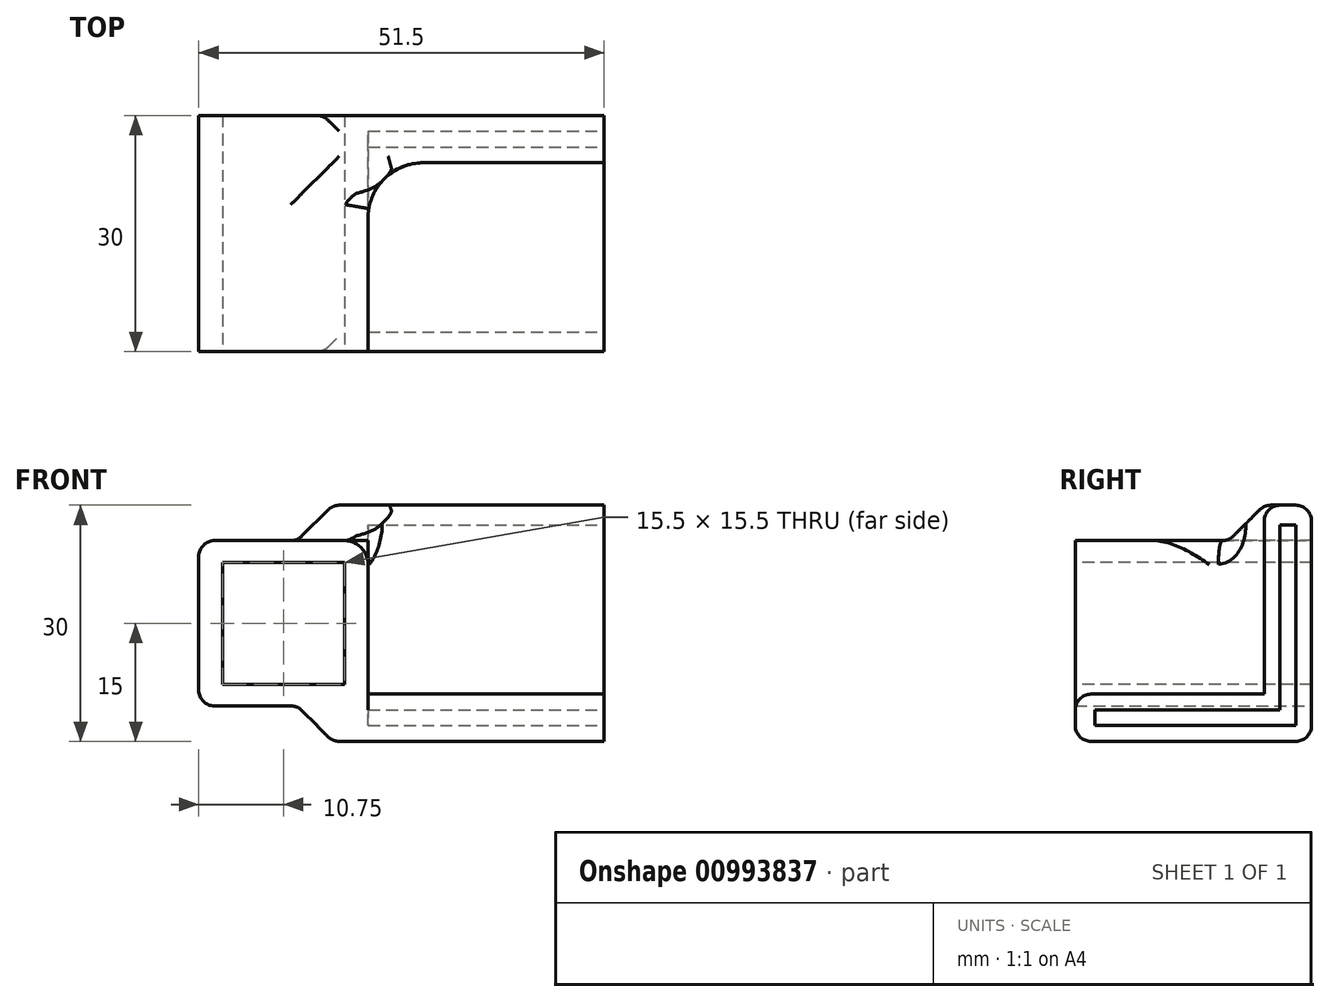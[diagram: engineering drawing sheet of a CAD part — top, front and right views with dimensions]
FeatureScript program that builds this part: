
annotation { "Feature Type Name" : "Feature", "Feature Type Description" : "" }
export const myFeature = defineFeature(function(context is Context, id is Id, definition is map)
    precondition{}
    {
        {
            var Q0;
            Q0=qCreatedBy(makeId("Top.planeOp"),FACE);
            var sketch = newSketch(context, id + "F0", { "sketchPlane" : qUnion([Q0])});
            skLineSegment(sketch, "E0", {"start": v(18, -44.27) * mm, "end": v(24, -44.27) * mm});
            skLineSegment(sketch, "E1", {"start": v(24, -44.27) * mm, "end": v(24, -14.27) * mm});
            skLineSegment(sketch, "E2", {"start": v(24, -14.27) * mm, "end": v(-12, -14.27) * mm});
            skLineSegment(sketch, "E3", {"start": v(-12, -14.27) * mm, "end": v(-12, -44.27) * mm});
            skLineSegment(sketch, "E4", {"start": v(-6, -44.27) * mm, "end": v(-6, -20.27) * mm});
            skLineSegment(sketch, "E5", {"start": v(-6, -20.27) * mm, "end": v(24, -20.27) * mm});
            skLineSegment(sketch, "E6", {"start": v(18, -44.27) * mm, "end": v(-12, -44.27) * mm});
            skSolve(sketch);
        }
        {
            var Q0;
            {var subQ2=sQuery(id+"F0.wireOp",EDGE,"E0");Q0=makeQuery(id+"F0.imprint","IMPRINT",FACE,{"disambiguationData":[TD([[makeQuery(id+"F0.imprint","IMPRINT",EDGE,{"derivedFrom":subQ2}),1.0]])]});}
            extrude(context, id + "F1", {"entities" : qUnion([Q0]), "depth" : 6 * mm, "offsetDistance" : 25 * mm});
        }
        {
            var Q0;
            {var subQ1=sQuery(id+"F0.wireOp",EDGE,"E2");Q0=makeQuery(id+"F0.imprint","IMPRINT",FACE,{"disambiguationData":[TD([[makeQuery(id+"F0.imprint","IMPRINT",EDGE,{"derivedFrom":subQ1}),1.0]])]});}
            extrude(context, id + "F2", {"entities" : qUnion([Q0]), "operationType" : NewBodyOperationType.ADD, "depth" : 30 * mm, "offsetDistance" : 25 * mm});
        }
        {
            var Q0;
            {var subQ0=sQuery(id+"F0.wireOp",EDGE,"E1");Q0=makeQuery(id+"F2.boolean.opBoolean","MERGE",FACE,{"derivedFrom":[makeQuery(id+"F1.opExtrude","SWEPT_FACE",FACE,{"disambiguationData":[OSD([subQ0])]}),makeQuery(id+"F2.opExtrude","SWEPT_FACE",FACE,{"disambiguationData":[OSD([subQ0])]})]});}
            var sketch = newSketch(context, id + "F3", { "sketchPlane" : qUnion([Q0])});
            skLineSegment(sketch, "E7", {"start": v(-41.77, 4) * mm, "end": v(-18.27, 4) * mm});
            skLineSegment(sketch, "E8", {"start": v(-18.27, 4) * mm, "end": v(-18.27, 27.5) * mm});
            skLineSegment(sketch, "E9", {"start": v(-18.27, 27.5) * mm, "end": v(-16.27, 27.5) * mm});
            skLineSegment(sketch, "E10", {"start": v(-16.27, 27.5) * mm, "end": v(-16.27, 2) * mm});
            skLineSegment(sketch, "E11", {"start": v(-16.27, 2) * mm, "end": v(-41.77, 2) * mm});
            skLineSegment(sketch, "E12", {"start": v(-41.77, 2) * mm, "end": v(-41.77, 4) * mm});
            skSolve(sketch);
        }
        {
            var Q0;
            Q0=makeQuery(id+"F3.imprint","IMPRINT",FACE,{"disambiguationData":[TD([[makeQuery(id+"F3.imprint","IMPRINT",EDGE,{"derivedFrom":sQuery(id+"F3.wireOp",EDGE,"E7")}),-1.0]])]});
            extrude(context, id + "F4", {"entities" : qUnion([Q0]), "operationType" : NewBodyOperationType.REMOVE, "oppositeDirection" : true, "depth" : 30 * mm, "offsetDistance" : 25 * mm});
        }
        {
            var Q0;
            Q0=makeQuery(id+"F2.opExtrude","SWEPT_FACE",FACE,{"disambiguationData":[OSD([sQuery(id+"F0.wireOp",EDGE,"E3")])]});
            extrude(context, id + "F5", {"entities" : qUnion([Q0]), "operationType" : NewBodyOperationType.ADD, "depth" : 20 * mm, "offsetDistance" : 25 * mm});
        }
        {
            var Q0;
            {var subQ0=sQuery(id+"F0.wireOp",EDGE,"E6");Q0=makeQuery(id+"F5.boolean.opBoolean","MERGE",FACE,{"derivedFrom":[makeQuery(id+"F2.boolean.opBoolean","MERGE",FACE,{"derivedFrom":[makeQuery(id+"F1.opExtrude","SWEPT_FACE",FACE,{"disambiguationData":[OSD([sQuery(id+"F0.wireOp",EDGE,"E0"),subQ0])]}),makeQuery(id+"F2.opExtrude","SWEPT_FACE",FACE,{"disambiguationData":[OSD([subQ0])]})]}),makeQuery(id+"F5.opExtrude","SWEPT_FACE",FACE,{"disambiguationData":[OSD([sQuery(id+"F0.wireOp",EDGE,"E3"),subQ0])]})]});}
            var sketch = newSketch(context, id + "F6", { "sketchPlane" : qUnion([Q0])});
            skLineSegment(sketch, "E13.bottom", {"start": v(-9, 7.25) * mm, "end": v(-24.5, 7.25) * mm});
            skLineSegment(sketch, "E13.top", {"start": v(-9, 22.75) * mm, "end": v(-24.5, 22.75) * mm});
            skLineSegment(sketch, "E13.left", {"start": v(-9, 7.25) * mm, "end": v(-9, 22.75) * mm});
            skLineSegment(sketch, "E13.right", {"start": v(-24.5, 7.25) * mm, "end": v(-24.5, 22.75) * mm});
            skPoint(sketch, "E13.middle", {"position": v(-16.75, 15) * mm});
            skLineSegment(sketch, "E14", {"start": v(-10.5, 25.5) * mm, "end": v(-10.5, 30) * mm});
            skLineSegment(sketch, "E15", {"start": v(-10.5, 25.5) * mm, "end": v(-27.5, 25.5) * mm});
            skLineSegment(sketch, "E16", {"start": v(-27.5, 25.5) * mm, "end": v(-27.5, 4.5) * mm});
            skLineSegment(sketch, "E17", {"start": v(-27.5, 4.5) * mm, "end": v(-10.5, 4.5) * mm});
            skLineSegment(sketch, "E18", {"start": v(-10.5, 4.5) * mm, "end": v(-10.5, 0) * mm});
            skLineSegment(sketch, "E19", {"start": v(-10.5, 0) * mm, "end": v(-32, 0) * mm});
            skLineSegment(sketch, "E20", {"start": v(-32, 0) * mm, "end": v(-32, 30) * mm});
            skLineSegment(sketch, "E21", {"start": v(-32, 30) * mm, "end": v(-10.5, 30) * mm});
            skLineSegment(sketch, "E22", {"start": v(-10.5, 25.5) * mm, "end": v(-6, 25.5) * mm});
            skLineSegment(sketch, "E23", {"start": v(-6, 25.5) * mm, "end": v(-6, 30) * mm});
            skLineSegment(sketch, "E24", {"start": v(-6, 30) * mm, "end": v(-10.5, 30) * mm});
            skSolve(sketch);
        }
        {
            var Q0;
            Q0=makeQuery(id+"F6.imprint","IMPRINT",FACE,{"disambiguationData":[TD([[makeQuery(id+"F6.imprint","IMPRINT",EDGE,{"derivedFrom":sQuery(id+"F6.wireOp",EDGE,"E13.bottom")}),-1.0]])]});
            var Q1;
            {var subQ0=sQuery(id+"F0.wireOp",EDGE,"E2");Q1=makeQuery(id+"F5.boolean.opBoolean","MERGE",FACE,{"derivedFrom":[makeQuery(id+"F2.opExtrude","SWEPT_FACE",FACE,{"disambiguationData":[OSD([subQ0])]}),makeQuery(id+"F5.opExtrude","SWEPT_FACE",FACE,{"disambiguationData":[OSD([subQ0,sQuery(id+"F0.wireOp",EDGE,"E3")])]})]});}
            extrude(context, id + "F7", {"entities" : qUnion([Q0]), "operationType" : NewBodyOperationType.REMOVE, "endBound" : BoundingType.UP_TO_SURFACE, "oppositeDirection" : true, "depth" : 25 * mm, "endBoundEntityFace" : qUnion([Q1]), "offsetDistance" : 25 * mm});
        }
        {
            var Q0;
            Q0=makeQuery(id+"F6.imprint","IMPRINT",FACE,{"disambiguationData":[TD([[makeQuery(id+"F6.imprint","IMPRINT",EDGE,{"derivedFrom":sQuery(id+"F6.wireOp",EDGE,"E14")}),1.0]])]});
            var Q1;
            {var subQ0=sQuery(id+"F0.wireOp",EDGE,"E2");Q1=makeQuery(id+"F5.boolean.opBoolean","MERGE",FACE,{"derivedFrom":[makeQuery(id+"F2.opExtrude","SWEPT_FACE",FACE,{"disambiguationData":[OSD([subQ0])]}),makeQuery(id+"F5.opExtrude","SWEPT_FACE",FACE,{"disambiguationData":[OSD([subQ0,sQuery(id+"F0.wireOp",EDGE,"E3")])]})]});}
            extrude(context, id + "F8", {"entities" : qUnion([Q0]), "operationType" : NewBodyOperationType.REMOVE, "endBound" : BoundingType.UP_TO_SURFACE, "oppositeDirection" : true, "depth" : 25 * mm, "endBoundEntityFace" : qUnion([Q1]), "offsetDistance" : 25 * mm});
        }
        {
            var Q0;
            Q0=makeQuery(id+"F6.imprint","IMPRINT",FACE,{"disambiguationData":[TD([[makeQuery(id+"F6.imprint","IMPRINT",EDGE,{"derivedFrom":sQuery(id+"F6.wireOp",EDGE,"E14")}),-1.0]])]});
            var Q1;
            Q1=makeQuery(id+"F2.opExtrude","SWEPT_FACE",FACE,{"disambiguationData":[OSD([sQuery(id+"F0.wireOp",EDGE,"E5")])]});
            extrude(context, id + "F9", {"entities" : qUnion([Q0]), "operationType" : NewBodyOperationType.REMOVE, "endBound" : BoundingType.UP_TO_SURFACE, "oppositeDirection" : true, "depth" : 22 * mm, "endBoundEntityFace" : qUnion([Q1]), "offsetDistance" : 25 * mm});
        }
        {
            var Q0;
            Q0=makeQuery(id+"F8.boolean.opBoolean","COPY",EDGE,{"derivedFrom":makeQuery(id+"F8.opExtrude","SWEPT_EDGE",EDGE,{"disambiguationData":[OSD([sQuery(id+"F6.wireOp",EDGE,"E14"),sQuery(id+"F6.wireOp",EDGE,"E15"),sQuery(id+"F6.wireOp",EDGE,"E22")])]})});
            var Q1;
            Q1=makeQuery(id+"F8.boolean.opBoolean","COPY",EDGE,{"derivedFrom":makeQuery(id+"F8.opExtrude","SWEPT_EDGE",EDGE,{"disambiguationData":[OSD([sQuery(id+"F6.wireOp",EDGE,"E17"),sQuery(id+"F6.wireOp",EDGE,"E18")])]})});
            var Q2;
            Q2=makeQuery(id+"F9.boolean.opBoolean","COPY",EDGE,{"derivedFrom":makeQuery(id+"F9.opExtrude","CAP_EDGE",EDGE,{"disambiguationData":[OSD([sQuery(id+"F6.wireOp",EDGE,"E22")])],"isStart":false})});
            chamfer(context, id + "F10", {"entities" : qUnion([Q0, Q1, Q2]), "width" : 4.5 * mm, "tangentPropagation" : true});
        }
        {
            var Q0;
            Q0=makeQuery(id+"F2.opExtrude","SWEPT_EDGE",EDGE,{"disambiguationData":[OSD([sQuery(id+"F0.wireOp",EDGE,"E4"),sQuery(id+"F0.wireOp",EDGE,"E5")])]});
            var Q1;
            Q1=makeQuery(id+"F1.opExtrude","CAP_EDGE",EDGE,{"disambiguationData":[OSD([sQuery(id+"F0.wireOp",EDGE,"E4")])],"isStart":false});
            var Q2;
            Q2=makeQuery(id+"F1.opExtrude","CAP_EDGE",EDGE,{"disambiguationData":[OSD([sQuery(id+"F0.wireOp",EDGE,"E5")])],"isStart":false});
            fillet(context, id + "F11", {"entities" : qUnion([Q0, Q1, Q2]), "radius" : 7 * mm, "tangentPropagation" : true, "allowEdgeOverflow" : false});
        }
        {
            var Q0;
            {var subQ0=sQuery(id+"F6.wireOp",EDGE,"E22");var subQ1=sQuery(id+"F6.wireOp",EDGE,"E15");Q0=makeQuery(id+"F10.opChamfer","BLEND_EDGE",EDGE,{"blendedFrom":[makeQuery(id+"F8.boolean.opBoolean","COPY",EDGE,{"derivedFrom":makeQuery(id+"F8.opExtrude","SWEPT_EDGE",EDGE,{"disambiguationData":[OSD([sQuery(id+"F6.wireOp",EDGE,"E14"),subQ1,subQ0])]})}),makeQuery(id+"F9.boolean.opBoolean","MERGE",FACE,{"derivedFrom":[makeQuery(id+"F8.boolean.opBoolean","COPY",FACE,{"derivedFrom":makeQuery(id+"F8.opExtrude","SWEPT_FACE",FACE,{"disambiguationData":[OSD([subQ1])]})})],"fromTools":[makeQuery(id+"F9.opExtrude","SWEPT_FACE",FACE,{"disambiguationData":[OSD([subQ0])]})]})],"blendedInto":[makeQuery(id+"F9.boolean.opBoolean","MERGE",FACE,{"derivedFrom":[makeQuery(id+"F8.boolean.opBoolean","COPY",FACE,{"derivedFrom":makeQuery(id+"F8.opExtrude","SWEPT_FACE",FACE,{"disambiguationData":[OSD([subQ1])]})})],"fromTools":[makeQuery(id+"F9.opExtrude","SWEPT_FACE",FACE,{"disambiguationData":[OSD([subQ0])]})]})]});}
            var Q1;
            {var subQ0=sQuery(id+"F6.wireOp",EDGE,"E22");Q1=makeQuery(id+"F10.opChamfer","BLEND_EDGE",EDGE,{"blendedFrom":[makeQuery(id+"F9.boolean.opBoolean","COPY",EDGE,{"derivedFrom":makeQuery(id+"F9.opExtrude","CAP_EDGE",EDGE,{"disambiguationData":[OSD([subQ0])],"isStart":false})}),makeQuery(id+"F9.boolean.opBoolean","MERGE",FACE,{"derivedFrom":[makeQuery(id+"F8.boolean.opBoolean","COPY",FACE,{"derivedFrom":makeQuery(id+"F8.opExtrude","SWEPT_FACE",FACE,{"disambiguationData":[OSD([sQuery(id+"F6.wireOp",EDGE,"E15")])]})})],"fromTools":[makeQuery(id+"F9.opExtrude","SWEPT_FACE",FACE,{"disambiguationData":[OSD([subQ0])]})]})],"blendedInto":[makeQuery(id+"F9.boolean.opBoolean","MERGE",FACE,{"derivedFrom":[makeQuery(id+"F8.boolean.opBoolean","COPY",FACE,{"derivedFrom":makeQuery(id+"F8.opExtrude","SWEPT_FACE",FACE,{"disambiguationData":[OSD([sQuery(id+"F6.wireOp",EDGE,"E15")])]})})],"fromTools":[makeQuery(id+"F9.opExtrude","SWEPT_FACE",FACE,{"disambiguationData":[OSD([subQ0])]})]})]});}
            var Q2;
            {var subQ0=sQuery(id+"F0.wireOp",EDGE,"E3");Q2=makeQuery(id+"F10.opChamfer","BLEND_EDGE",EDGE,{"blendedFrom":[makeQuery(id+"F9.boolean.opBoolean","COPY",EDGE,{"derivedFrom":makeQuery(id+"F9.opExtrude","CAP_EDGE",EDGE,{"disambiguationData":[OSD([sQuery(id+"F6.wireOp",EDGE,"E22")])],"isStart":false})}),makeQuery(id+"F5.boolean.opBoolean","MERGE",FACE,{"derivedFrom":[makeQuery(id+"F2.opExtrude","CAP_FACE",FACE,{"disambiguationData":[OSD([sQuery(id+"F0.wireOp",EDGE,"E1"),sQuery(id+"F0.wireOp",EDGE,"E2"),subQ0,sQuery(id+"F0.wireOp",EDGE,"E4"),sQuery(id+"F0.wireOp",EDGE,"E5"),sQuery(id+"F0.wireOp",EDGE,"E6")])],"isStart":false}),makeQuery(id+"F5.opExtrude","SWEPT_FACE",FACE,{"disambiguationData":[OSD([subQ0]),TDD([makeQuery(id+"F2.opExtrude","CAP_EDGE",EDGE,{"disambiguationData":[OSD([subQ0])],"isStart":false})])]})]})],"blendedInto":[makeQuery(id+"F5.boolean.opBoolean","MERGE",FACE,{"derivedFrom":[makeQuery(id+"F2.opExtrude","CAP_FACE",FACE,{"disambiguationData":[OSD([sQuery(id+"F0.wireOp",EDGE,"E1"),sQuery(id+"F0.wireOp",EDGE,"E2"),subQ0,sQuery(id+"F0.wireOp",EDGE,"E4"),sQuery(id+"F0.wireOp",EDGE,"E5"),sQuery(id+"F0.wireOp",EDGE,"E6")])],"isStart":false}),makeQuery(id+"F5.opExtrude","SWEPT_FACE",FACE,{"disambiguationData":[OSD([subQ0]),TDD([makeQuery(id+"F2.opExtrude","CAP_EDGE",EDGE,{"disambiguationData":[OSD([subQ0])],"isStart":false})])]})]})]});}
            var Q3;
            {var subQ0=sQuery(id+"F0.wireOp",EDGE,"E3");Q3=makeQuery(id+"F10.opChamfer","BLEND_EDGE",EDGE,{"blendedFrom":[makeQuery(id+"F8.boolean.opBoolean","COPY",EDGE,{"derivedFrom":makeQuery(id+"F8.opExtrude","SWEPT_EDGE",EDGE,{"disambiguationData":[OSD([sQuery(id+"F6.wireOp",EDGE,"E14"),sQuery(id+"F6.wireOp",EDGE,"E15"),sQuery(id+"F6.wireOp",EDGE,"E22")])]})}),makeQuery(id+"F5.boolean.opBoolean","MERGE",FACE,{"derivedFrom":[makeQuery(id+"F2.opExtrude","CAP_FACE",FACE,{"disambiguationData":[OSD([sQuery(id+"F0.wireOp",EDGE,"E1"),sQuery(id+"F0.wireOp",EDGE,"E2"),subQ0,sQuery(id+"F0.wireOp",EDGE,"E4"),sQuery(id+"F0.wireOp",EDGE,"E5"),sQuery(id+"F0.wireOp",EDGE,"E6")])],"isStart":false}),makeQuery(id+"F5.opExtrude","SWEPT_FACE",FACE,{"disambiguationData":[OSD([subQ0]),TDD([makeQuery(id+"F2.opExtrude","CAP_EDGE",EDGE,{"disambiguationData":[OSD([subQ0])],"isStart":false})])]})]})],"blendedInto":[makeQuery(id+"F5.boolean.opBoolean","MERGE",FACE,{"derivedFrom":[makeQuery(id+"F2.opExtrude","CAP_FACE",FACE,{"disambiguationData":[OSD([sQuery(id+"F0.wireOp",EDGE,"E1"),sQuery(id+"F0.wireOp",EDGE,"E2"),subQ0,sQuery(id+"F0.wireOp",EDGE,"E4"),sQuery(id+"F0.wireOp",EDGE,"E5"),sQuery(id+"F0.wireOp",EDGE,"E6")])],"isStart":false}),makeQuery(id+"F5.opExtrude","SWEPT_FACE",FACE,{"disambiguationData":[OSD([subQ0]),TDD([makeQuery(id+"F2.opExtrude","CAP_EDGE",EDGE,{"disambiguationData":[OSD([subQ0])],"isStart":false})])]})]})]});}
            var Q4;
            {var subQ0=sQuery(id+"F0.wireOp",EDGE,"E3");var subQ1=sQuery(id+"F0.wireOp",EDGE,"E2");Q4=makeQuery(id+"F5.boolean.opBoolean","MERGE",EDGE,{"derivedFrom":[makeQuery(id+"F2.opExtrude","CAP_EDGE",EDGE,{"disambiguationData":[OSD([subQ1])],"isStart":false}),makeQuery(id+"F5.opExtrude","SWEPT_EDGE",EDGE,{"disambiguationData":[OSD([subQ1,subQ0]),TDD([makeQuery(id+"F2.opExtrude","CAP_VERTEX",VERTEX,{"disambiguationData":[OSD([subQ1,subQ0])],"isStart":false})])]})]});}
            var Q5;
            Q5=makeQuery(id+"F9.boolean.opBoolean","MERGE",EDGE,{"derivedFrom":[makeQuery(id+"F2.opExtrude","CAP_EDGE",EDGE,{"disambiguationData":[OSD([sQuery(id+"F0.wireOp",EDGE,"E5")])],"isStart":false})],"fromTools":[makeQuery(id+"F9.opExtrude","CAP_EDGE",EDGE,{"disambiguationData":[OSD([sQuery(id+"F6.wireOp",EDGE,"E24")])],"isStart":false})]});
            var Q6;
            Q6=makeQuery(id+"F1.opExtrude","CAP_EDGE",EDGE,{"disambiguationData":[OSD([sQuery(id+"F0.wireOp",EDGE,"E0"),sQuery(id+"F0.wireOp",EDGE,"E6")])],"isStart":false});
            var Q7;
            Q7=makeQuery(id+"F8.boolean.opBoolean","COPY",EDGE,{"derivedFrom":makeQuery(id+"F8.opExtrude","SWEPT_EDGE",EDGE,{"disambiguationData":[OSD([sQuery(id+"F6.wireOp",EDGE,"E15"),sQuery(id+"F6.wireOp",EDGE,"E16")])]})});
            var Q8;
            Q8=makeQuery(id+"F8.boolean.opBoolean","COPY",EDGE,{"derivedFrom":makeQuery(id+"F8.opExtrude","SWEPT_EDGE",EDGE,{"disambiguationData":[OSD([sQuery(id+"F6.wireOp",EDGE,"E16"),sQuery(id+"F6.wireOp",EDGE,"E17")])]})});
            var Q9;
            {var subQ0=sQuery(id+"F0.wireOp",EDGE,"E3");var subQ1=sQuery(id+"F0.wireOp",EDGE,"E2");Q9=makeQuery(id+"F5.boolean.opBoolean","MERGE",EDGE,{"derivedFrom":[makeQuery(id+"F2.opExtrude","CAP_EDGE",EDGE,{"disambiguationData":[OSD([subQ1])],"isStart":true}),makeQuery(id+"F5.opExtrude","SWEPT_EDGE",EDGE,{"disambiguationData":[OSD([subQ1,subQ0]),TDD([makeQuery(id+"F2.opExtrude","CAP_VERTEX",VERTEX,{"disambiguationData":[OSD([subQ1,subQ0])],"isStart":true})])]})]});}
            var Q10;
            {var subQ0=sQuery(id+"F6.wireOp",EDGE,"E17");Q10=makeQuery(id+"F10.opChamfer","BLEND_EDGE",EDGE,{"blendedFrom":[makeQuery(id+"F8.boolean.opBoolean","COPY",EDGE,{"derivedFrom":makeQuery(id+"F8.opExtrude","SWEPT_EDGE",EDGE,{"disambiguationData":[OSD([subQ0,sQuery(id+"F6.wireOp",EDGE,"E18")])]})}),makeQuery(id+"F8.boolean.opBoolean","COPY",FACE,{"derivedFrom":makeQuery(id+"F8.opExtrude","SWEPT_FACE",FACE,{"disambiguationData":[OSD([subQ0])]})})],"blendedInto":[makeQuery(id+"F8.boolean.opBoolean","COPY",FACE,{"derivedFrom":makeQuery(id+"F8.opExtrude","SWEPT_FACE",FACE,{"disambiguationData":[OSD([subQ0])]})})]});}
            var Q11;
            {var subQ0=sQuery(id+"F0.wireOp",EDGE,"E6");var subQ1=sQuery(id+"F0.wireOp",EDGE,"E3");Q11=makeQuery(id+"F5.boolean.opBoolean","MERGE",EDGE,{"derivedFrom":[makeQuery(id+"F2.boolean.opBoolean","MERGE",EDGE,{"derivedFrom":[makeQuery(id+"F1.opExtrude","CAP_EDGE",EDGE,{"disambiguationData":[OSD([sQuery(id+"F0.wireOp",EDGE,"E0"),subQ0])],"isStart":true}),makeQuery(id+"F2.opExtrude","CAP_EDGE",EDGE,{"disambiguationData":[OSD([subQ0])],"isStart":true})]}),makeQuery(id+"F5.opExtrude","SWEPT_EDGE",EDGE,{"disambiguationData":[OSD([subQ1,subQ0]),TDD([makeQuery(id+"F2.opExtrude","CAP_VERTEX",VERTEX,{"disambiguationData":[OSD([subQ1,subQ0])],"isStart":true})])]})]});}
            var Q12;
            {var subQ0=sQuery(id+"F0.wireOp",EDGE,"E3");var subQ1=sQuery(id+"F0.wireOp",EDGE,"E6");var subQ2=sQuery(id+"F0.wireOp",EDGE,"E5");var subQ3=sQuery(id+"F0.wireOp",EDGE,"E4");var subQ4=sQuery(id+"F0.wireOp",EDGE,"E1");Q12=makeQuery(id+"F10.opChamfer","BLEND_EDGE",EDGE,{"blendedFrom":[makeQuery(id+"F8.boolean.opBoolean","COPY",EDGE,{"derivedFrom":makeQuery(id+"F8.opExtrude","SWEPT_EDGE",EDGE,{"disambiguationData":[OSD([sQuery(id+"F6.wireOp",EDGE,"E17"),sQuery(id+"F6.wireOp",EDGE,"E18")])]})}),makeQuery(id+"F5.boolean.opBoolean","MERGE",FACE,{"derivedFrom":[makeQuery(id+"F2.boolean.opBoolean","MERGE",FACE,{"derivedFrom":[makeQuery(id+"F1.opExtrude","CAP_FACE",FACE,{"disambiguationData":[OSD([sQuery(id+"F0.wireOp",EDGE,"E0"),subQ4,subQ3,subQ2,subQ1])],"isStart":true}),makeQuery(id+"F2.opExtrude","CAP_FACE",FACE,{"disambiguationData":[OSD([subQ4,sQuery(id+"F0.wireOp",EDGE,"E2"),subQ0,subQ3,subQ2,subQ1])],"isStart":true})]}),makeQuery(id+"F5.opExtrude","SWEPT_FACE",FACE,{"disambiguationData":[OSD([subQ0]),TDD([makeQuery(id+"F2.opExtrude","CAP_EDGE",EDGE,{"disambiguationData":[OSD([subQ0])],"isStart":true})])]})]})],"blendedInto":[makeQuery(id+"F5.boolean.opBoolean","MERGE",FACE,{"derivedFrom":[makeQuery(id+"F2.boolean.opBoolean","MERGE",FACE,{"derivedFrom":[makeQuery(id+"F1.opExtrude","CAP_FACE",FACE,{"disambiguationData":[OSD([sQuery(id+"F0.wireOp",EDGE,"E0"),subQ4,subQ3,subQ2,subQ1])],"isStart":true}),makeQuery(id+"F2.opExtrude","CAP_FACE",FACE,{"disambiguationData":[OSD([subQ4,sQuery(id+"F0.wireOp",EDGE,"E2"),subQ0,subQ3,subQ2,subQ1])],"isStart":true})]}),makeQuery(id+"F5.opExtrude","SWEPT_FACE",FACE,{"disambiguationData":[OSD([subQ0]),TDD([makeQuery(id+"F2.opExtrude","CAP_EDGE",EDGE,{"disambiguationData":[OSD([subQ0])],"isStart":true})])]})]})]});}
            fillet(context, id + "F12", {"entities" : qUnion([Q0, Q1, Q2, Q3, Q4, Q5, Q6, Q7, Q8, Q9, Q10, Q11, Q12]), "radius" : 2 * mm, "tangentPropagation" : true, "allowEdgeOverflow" : false});
        }
        {
            var Q0;
            Q0=makeQuery(id+"F9.boolean.opBoolean","COPY",EDGE,{"derivedFrom":makeQuery(id+"F9.opExtrude","SWEPT_EDGE",EDGE,{"disambiguationData":[OSD([sQuery(id+"F0.wireOp",EDGE,"E4"),sQuery(id+"F0.wireOp",EDGE,"E6"),sQuery(id+"F6.wireOp",EDGE,"E22"),sQuery(id+"F6.wireOp",EDGE,"E23")])]})});
            var Q1;
            Q1=makeQuery(id+"F11.opFillet","BLEND_EDGE",EDGE,{"blendedFrom":[makeQuery(id+"F2.opExtrude","SWEPT_EDGE",EDGE,{"disambiguationData":[OSD([sQuery(id+"F0.wireOp",EDGE,"E4"),sQuery(id+"F0.wireOp",EDGE,"E5")])]}),makeQuery(id+"F9.boolean.opBoolean","MERGE",FACE,{"derivedFrom":[makeQuery(id+"F8.boolean.opBoolean","COPY",FACE,{"derivedFrom":makeQuery(id+"F8.opExtrude","SWEPT_FACE",FACE,{"disambiguationData":[OSD([sQuery(id+"F6.wireOp",EDGE,"E15")])]})})],"fromTools":[makeQuery(id+"F9.opExtrude","SWEPT_FACE",FACE,{"disambiguationData":[OSD([sQuery(id+"F6.wireOp",EDGE,"E22")])]})]})],"blendedInto":[makeQuery(id+"F9.boolean.opBoolean","MERGE",FACE,{"derivedFrom":[makeQuery(id+"F8.boolean.opBoolean","COPY",FACE,{"derivedFrom":makeQuery(id+"F8.opExtrude","SWEPT_FACE",FACE,{"disambiguationData":[OSD([sQuery(id+"F6.wireOp",EDGE,"E15")])]})})],"fromTools":[makeQuery(id+"F9.opExtrude","SWEPT_FACE",FACE,{"disambiguationData":[OSD([sQuery(id+"F6.wireOp",EDGE,"E22")])]})]})]});
            var Q2;
            {var subQ0=sQuery(id+"F0.wireOp",EDGE,"E5");var subQ1=sQuery(id+"F0.wireOp",EDGE,"E4");var subQ2=sQuery(id+"F6.wireOp",EDGE,"E22");Q2=makeQuery(id+"F12.opFillet","BLEND_EDGE",EDGE,{"blendedFrom":[makeQuery(id+"F10.opChamfer","BLEND_EDGE",EDGE,{"blendedFrom":[makeQuery(id+"F9.boolean.opBoolean","COPY",EDGE,{"derivedFrom":makeQuery(id+"F9.opExtrude","CAP_EDGE",EDGE,{"disambiguationData":[OSD([subQ2])],"isStart":false})}),makeQuery(id+"F9.boolean.opBoolean","MERGE",FACE,{"derivedFrom":[makeQuery(id+"F8.boolean.opBoolean","COPY",FACE,{"derivedFrom":makeQuery(id+"F8.opExtrude","SWEPT_FACE",FACE,{"disambiguationData":[OSD([sQuery(id+"F6.wireOp",EDGE,"E15")])]})})],"fromTools":[makeQuery(id+"F9.opExtrude","SWEPT_FACE",FACE,{"disambiguationData":[OSD([subQ2])]})]})],"blendedInto":[makeQuery(id+"F9.boolean.opBoolean","MERGE",FACE,{"derivedFrom":[makeQuery(id+"F8.boolean.opBoolean","COPY",FACE,{"derivedFrom":makeQuery(id+"F8.opExtrude","SWEPT_FACE",FACE,{"disambiguationData":[OSD([sQuery(id+"F6.wireOp",EDGE,"E15")])]})})],"fromTools":[makeQuery(id+"F9.opExtrude","SWEPT_FACE",FACE,{"disambiguationData":[OSD([subQ2])]})]})]}),makeQuery(id+"F11.opFillet","BLEND_FACE",FACE,{"disambiguationData":[OSD([subQ1,subQ0]),TDD([makeQuery(id+"F2.opExtrude","SWEPT_EDGE",EDGE,{"disambiguationData":[OSD([subQ1,subQ0])]})])]})],"blendedInto":[makeQuery(id+"F11.opFillet","BLEND_FACE",FACE,{"disambiguationData":[OSD([subQ1,subQ0]),TDD([makeQuery(id+"F2.opExtrude","SWEPT_EDGE",EDGE,{"disambiguationData":[OSD([subQ1,subQ0])]})])]})]});}
            fillet(context, id + "F13", {"entities" : qUnion([Q0, Q1, Q2]), "radius" : 3 * mm, "allowEdgeOverflow" : false});
        }
    });
